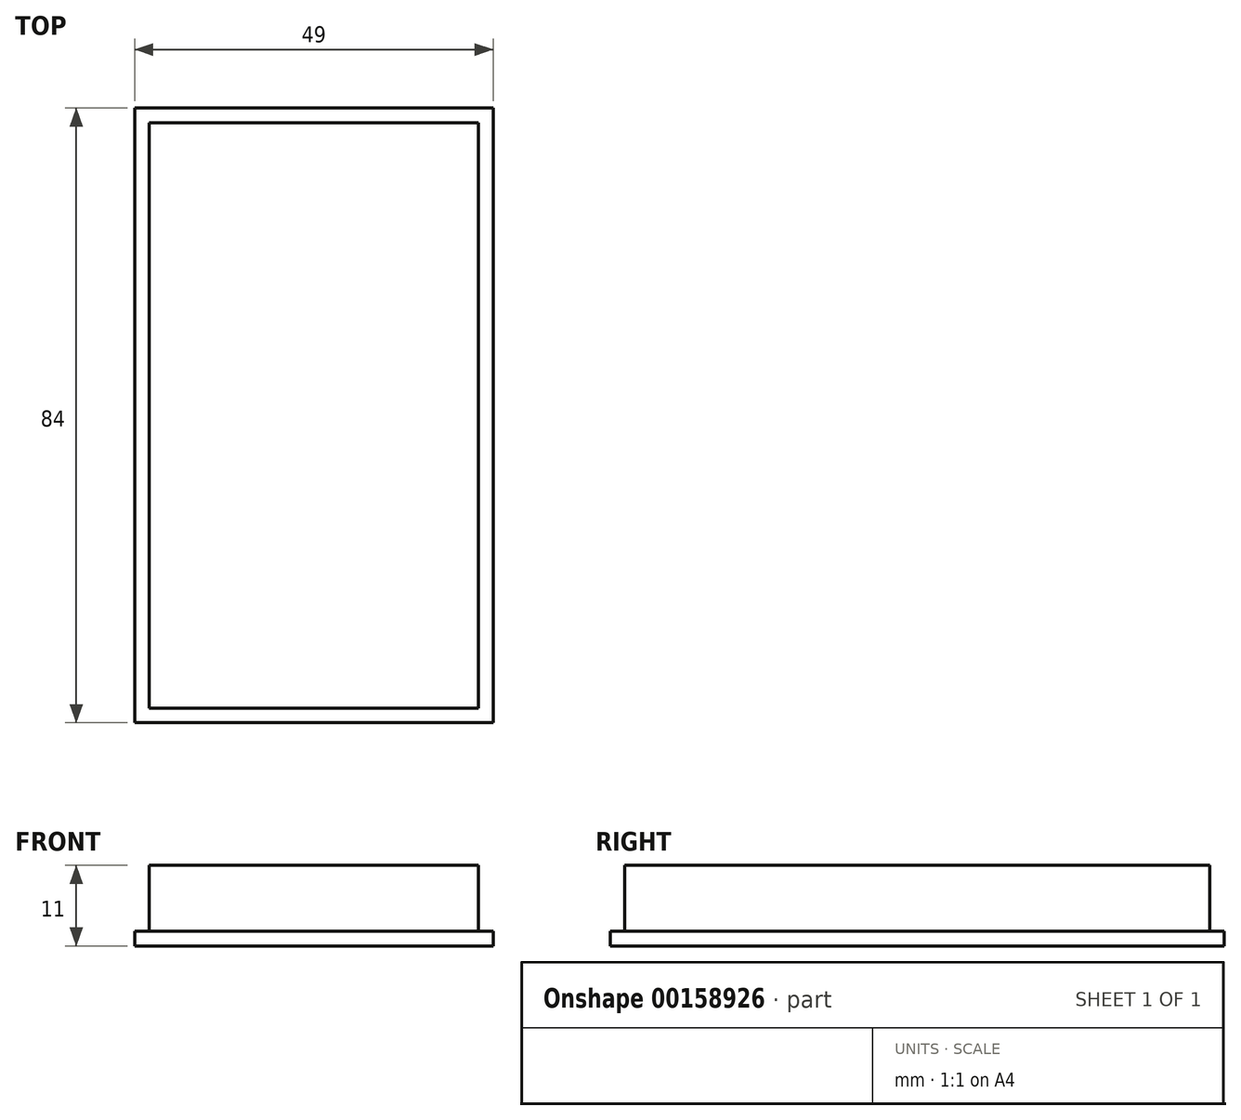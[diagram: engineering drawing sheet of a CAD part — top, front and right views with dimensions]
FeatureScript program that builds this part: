
annotation { "Feature Type Name" : "Feature", "Feature Type Description" : "" }
export const myFeature = defineFeature(function(context is Context, id is Id, definition is map)
    precondition{}
    {
        {
            var Q0;
            Q0=qCreatedBy(makeId("Top.planeOp"),FACE);
            var sketch = newSketch(context, id + "F0", { "sketchPlane" : qUnion([Q0])});
            skLineSegment(sketch, "E0.bottom", {"start": v(-21.14, -38.25) * mm, "end": v(23.86, -38.25) * mm});
            skLineSegment(sketch, "E0.top", {"start": v(-21.14, 41.75) * mm, "end": v(23.86, 41.75) * mm});
            skLineSegment(sketch, "E0.left", {"start": v(-21.14, -38.25) * mm, "end": v(-21.14, 41.75) * mm});
            skLineSegment(sketch, "E0.right", {"start": v(23.86, -38.25) * mm, "end": v(23.86, 41.75) * mm});
            skSolve(sketch);
        }
        {
            var Q0;
            Q0=makeQuery(id+"F0.imprint","IMPRINT",FACE,{"disambiguationData":[TD([[makeQuery(id+"F0.imprint","IMPRINT",EDGE,{"derivedFrom":sQuery(id+"F0.wireOp",EDGE,"E0.bottom")}),1.0]])]});
            extrude(context, id + "F1", {"entities" : qUnion([Q0]), "depth" : 9 * mm});
        }
        {
            var Q0;
            Q0=qCreatedBy(makeId("Top.planeOp"),FACE);
            var sketch = newSketch(context, id + "F2", { "sketchPlane" : qUnion([Q0])});
            skLineSegment(sketch, "E1.bottom", {"start": v(-23.14, 43.75) * mm, "end": v(25.86, 43.75) * mm});
            skLineSegment(sketch, "E1.top", {"start": v(-23.14, -40.25) * mm, "end": v(25.86, -40.25) * mm});
            skLineSegment(sketch, "E1.left", {"start": v(-23.14, 43.75) * mm, "end": v(-23.14, -40.25) * mm});
            skLineSegment(sketch, "E1.right", {"start": v(25.86, 43.75) * mm, "end": v(25.86, -40.25) * mm});
            skSolve(sketch);
        }
        {
            var Q0;
            Q0 = qSketchRegion(id + "F2", true);
            extrude(context, id + "F3", {"entities" : qUnion([Q0]), "oppositeDirection" : true, "depth" : 2 * mm});
        }
    });
